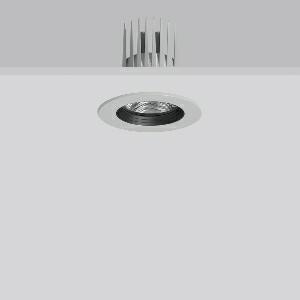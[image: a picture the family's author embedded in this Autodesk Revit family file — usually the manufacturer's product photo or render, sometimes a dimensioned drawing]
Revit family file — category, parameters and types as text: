
# Revit family: heledon_mini_e_901742_004_1_76_8c28
name_source: partatom
category: Lighting Fixtures
units: mm (PartAtom-declared; Revit-internal decimal feet)

## family parameters
Cut with Voids When Loaded = No
Host = Face
Light Source = No
Part Type = Normal
Room Calculation Point = No
Round Connector Dimension = Use Diameter
Shared = No

## types (1)
- HELEDON mini E (1 x LED Modul 940, 2750 lm, 4000)
    Apparent Load = 20 VA
    Approval mark = CE
    CIE Flux Codes = 95 99 100 100 100
    Color Rendering = 92
    Color Temperature = 4000
    Default Elevation = 1800 mm
    Description = Series: HELEDON mini
Round recessed downlight. Housing: die-cast aluminium, powder-coated. Black plastic ring and recessed LED to prevent glare from the side. Optical assembly with reflector made of MIRO-Silver with 98% total light reflection for outstanding efficiency - can be changed without tools. Best colour rendering index Ra>90. Suitable for Recessed ceiling mounting. Installation without tools thanks to spring fastening system. Including separate LED converter with connecting cable 600 mm.High quality converter without flickering and stroboscopic effect. Through-wiring box (5 pole) available as accessory. The following accessories can be mounted without use of tools: interchangeable lenses, decorative glasses, honeycomb louvre, clear and frosted diffusers, white interchangeable plastic ring. 
Colour: silver
Diameter: 124 mm
Height: 3 mm
Cut-out diameter: 114 mm
Recess height: 170 mm
Luminaire: recess height: 120 mm
Lamp: LED
Socket: without socket
Colour temperature: 4000K
Colour rendering index (CRI): 92
System power: 20 W
Rated luminous flux: 2750 lm
Luminous efficiency: 138 lm/W
Control gear: Converter, dimmable, DALI
Protection class: II
Type of protection: IP 20
    Height = 0 mm  [stored 0 ft]
    Lamp = 1 x LED Modul 940
    Lamp Light Flux = 2750 lm
    Lamp count = 1
    Length = 124 mm  [stored 0.406824 ft]
    Lifetime = 50000 h
    Luminous efficacy = 138 lm/W
    Manufacturer = RZB
    ModVariant = No
    Model = 901742.004.1.76
    Mounting Place = Ceiling
    Mounting Type = Recessed
    Number of Poles = 1
    OnlyDefault = Yes
    Power Factor = 1
    Product Name = HELEDON mini E
    Product group = Recessed downlights
    ProductGroupID = 402
    Protection Class = Protection class II
    Protection Degree = IP 20
    RLX_Detail_Level = 1
    RLX_Emergency_Light_Flux = 0 lm
    RLX_Emergency_Type = 0
    RLX_Emergency_Type_DB = No
    RlxData = <blob elided: 126057 chars, md5=76782c58>
    Socket = socket
    Standby Power = 0 W
    System Light Flux = 2750 lm
    System Power = 20 W
    Type Comments = Product without accessories
    Type Image = 901657.004.jpg
    URL = http://relux.com
    VarID = ---
    Voltage = 230 V
    Voltage Range = 220-240 V
    Weight = 0.00 kg
    Width = 0 mm  [stored 0 ft]

note: [stored X ft] marks values corroborated as IEEE doubles in the binary element streams (Revit-internal decimal feet)

## geometry (parser evidence)
native form markers: Blend x4, Sweep x10
no freeform markers — native parametric forms only
